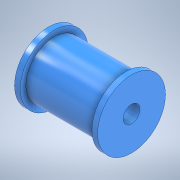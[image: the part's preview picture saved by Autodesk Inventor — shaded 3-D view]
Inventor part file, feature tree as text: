
AUTODESK INVENTOR PART (.ipt)
format: ipt  version: 2020 (Build 240168000, 168)  size: 128,512 bytes
history: native  units: in
note: dims shown in document units (in); Inventor stores cm internally (conversion verified against a paired STEP export)
features: extrude x2, sketch x2, mirror x1
ambient origin geometry x8: Origin, YZ Plane, XZ Plane, XY Plane, X Axis, Y Axis, Z Axis, Center Point
bodies: Solid1 (feature_tree)
feature tree (5):
  extrude  "Extrusion1"  Depth=0.3937in
  extrude  "Extrusion2"  Depth=0.0394in
  mirror  "Mirror1"
  sketch  "Sketch1"  dims[d0=0.1181in d1=0.3937in]
  sketch  "Sketch2"  dims[d2=0.5in d3=0.0in d4=0.4724in d5=0.1181in d6=0.0394in d7=0.0in]
